# Revit family: ATELIS Concrete Basin_RFA
name_source: partatom
category: Generic Models
units: mm (PartAtom-declared; Revit-internal decimal feet)

## family parameters
Always vertical = Yes
Can host rebar = No
Cut with Voids When Loaded = No
Maintain Annotation Orientation = No
OmniClass Number = 23.31.13.11
Part Type = Normal
Room Calculation Point = No
Round Connector Dimension = Use Diameter
Shared = No
Work Plane-Based = No

## types (1)
- ATELIS Concrete Basin
    Almond-SKU = 15513
    Black-SKU = 0
    Brass-SKU = 0
    Chrome-SKU = 0
    Copper-SKU = 0
    DarkGrey-SKU = 15514
    Default Elevation = 0 mm  [stored 0 ft]
    Description = ATELIS Concrete Basin
    Gunmetal-SKU = 0
    Manufacturer = ABI Interiors PTY LTD
    Nickel-SKU = 0
    StainlessSteel-SKU = 0
    White-SKU = 15512

note: [stored X ft] marks values corroborated as IEEE doubles in the binary element streams (Revit-internal decimal feet)

## geometry (parser evidence)
native form markers: Sweep x3
no freeform markers — native parametric forms only
